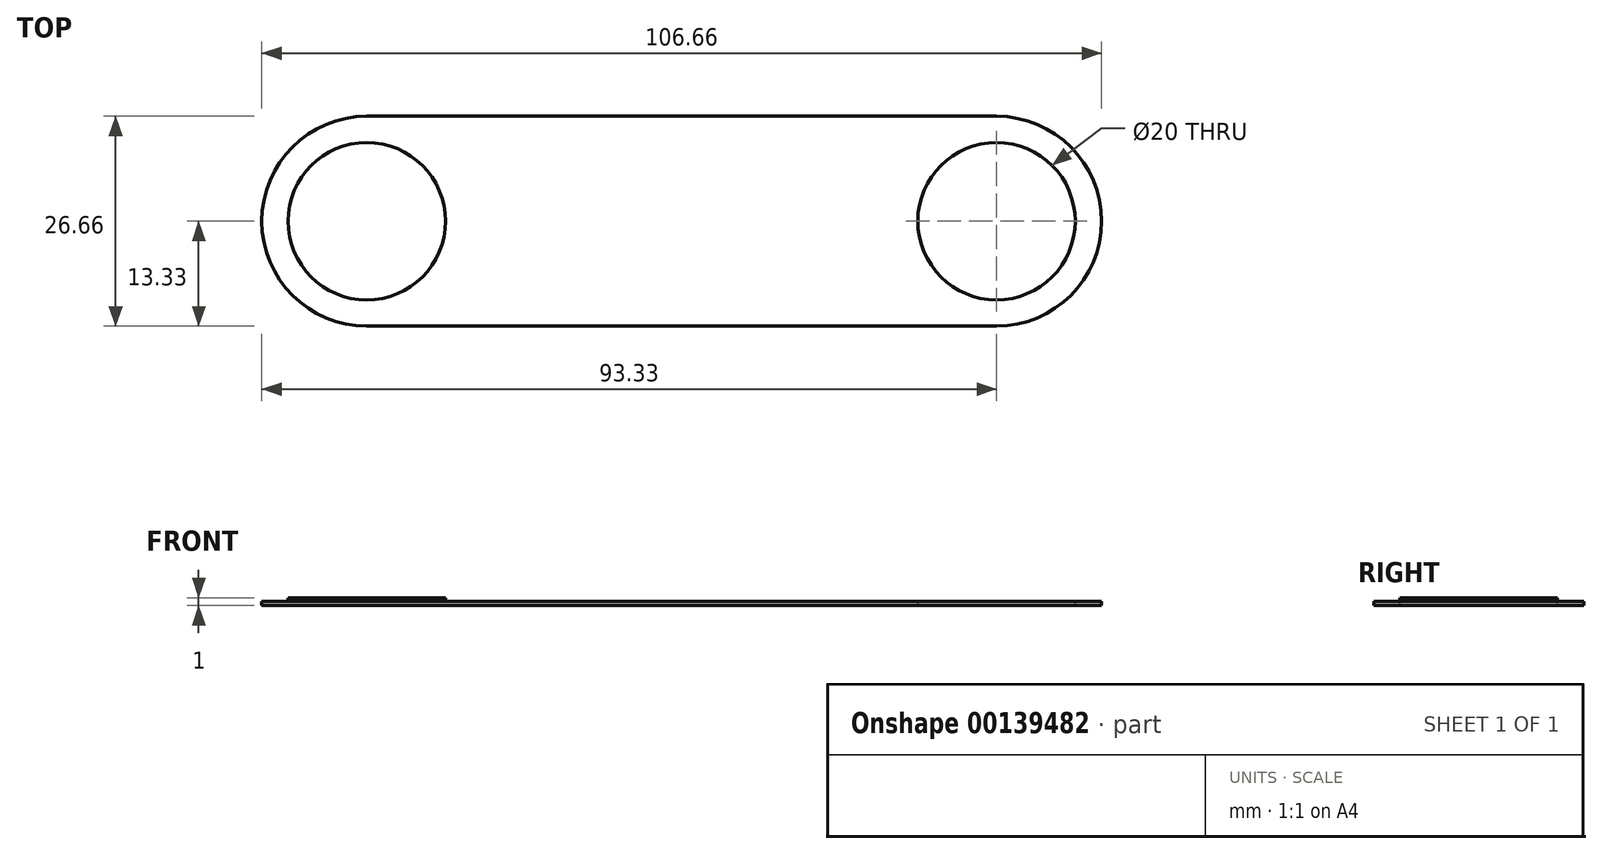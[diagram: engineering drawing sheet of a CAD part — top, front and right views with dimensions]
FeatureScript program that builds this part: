
annotation { "Feature Type Name" : "Feature", "Feature Type Description" : "" }
export const myFeature = defineFeature(function(context is Context, id is Id, definition is map)
    precondition{}
    {
        {
            assignVariable(context, id + "F0", {"name" : "depth", "anyValue" : .5});
        }
        {
            var Q0;
            Q0=qCreatedBy(makeId("Top.planeOp"),FACE);
            var sketch = newSketch(context, id + "F1", { "sketchPlane" : qUnion([Q0])});
            skLineSegment(sketch, "E0.bottom", {"start": v(40, 13.33) * mm, "end": v(-40, 13.33) * mm});
            skLineSegment(sketch, "E0.top", {"start": v(40, -13.33) * mm, "end": v(-40, -13.33) * mm});
            skPoint(sketch, "E0.middle", {"position": v(0, 0) * mm});
            skArc(sketch, "E1", {"start": v(-40, 13.33) * mm, "mid": v(-53.33, 0) * mm, "end": v(-40, -13.33) * mm});
            skArc(sketch, "E2", {"start": v(40, -13.33) * mm, "mid": v(53.33, 0) * mm, "end": v(40, 13.33) * mm});
            skSolve(sketch);
        }
        {
            var Q0;
            Q0=makeQuery(id+"F1.imprint","IMPRINT",FACE,{"disambiguationData":[TD([[makeQuery(id+"F1.imprint","IMPRINT",EDGE,{"derivedFrom":sQuery(id+"F1.wireOp",EDGE,"E0.bottom")}),1.0]])]});
            extrude(context, id + "F2", {"entities" : qUnion([Q0]), "depth" : (getVariable(context, 'depth')) * mm});
        }
        {
            var Q0;
            Q0=makeQuery(id+"F2.opExtrude","CAP_FACE",FACE,{"disambiguationData":[OSD([sQuery(id+"F1.wireOp",EDGE,"E0.bottom"),sQuery(id+"F1.wireOp",EDGE,"E0.top"),sQuery(id+"F1.wireOp",EDGE,"E1"),sQuery(id+"F1.wireOp",EDGE,"E2")])],"isStart":false});
            var sketch = newSketch(context, id + "F3", { "sketchPlane" : qUnion([Q0])});
            skCircle(sketch, "E3", {"center": v(-40, 0) * mm, "radius": 10 * mm});
            skCircle(sketch, "E4", {"center": v(40, 0) * mm, "radius": 10 * mm});
            skSolve(sketch);
        }
        {
            var Q0;
            Q0=makeQuery(id+"F3.imprint","IMPRINT",FACE,{"disambiguationData":[TD([[makeQuery(id+"F3.imprint","IMPRINT",EDGE,{"derivedFrom":sQuery(id+"F3.wireOp",EDGE,"E4")}),1.0]])]});
            extrude(context, id + "F4", {"entities" : qUnion([Q0]), "operationType" : NewBodyOperationType.REMOVE, "oppositeDirection" : true, "depth" : (getVariable(context, 'depth')) * mm});
        }
        {
            var Q0;
            Q0=makeQuery(id+"F3.imprint","IMPRINT",FACE,{"disambiguationData":[TD([[makeQuery(id+"F3.imprint","IMPRINT",EDGE,{"derivedFrom":sQuery(id+"F3.wireOp",EDGE,"E3")}),1.0]])]});
            extrude(context, id + "F5", {"entities" : qUnion([Q0]), "operationType" : NewBodyOperationType.ADD, "depth" : (getVariable(context, 'depth')) * mm});
        }
    });
